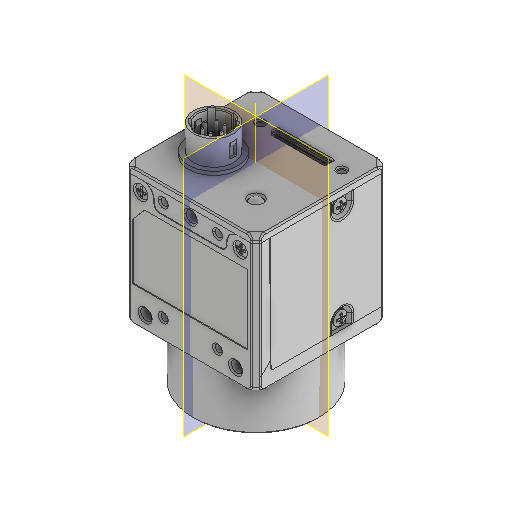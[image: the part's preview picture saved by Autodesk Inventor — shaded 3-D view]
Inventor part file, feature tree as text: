
AUTODESK INVENTOR PART (.ipt)
format: ipt  version: 2024.1 (Build 281209000, 209)  size: 3,227,136 bytes
history: native  units: mm
features: plane x2, other x1, imported_body x1
ambient origin geometry x8: Origin, YZ Plane, XZ Plane, XY Plane, X Axis, Y Axis, Z Axis, Center Point
bodies: Volumenkörper1 (feature_tree)
feature tree (4):
  plane  "Arbeitsebene1"
  plane  "Arbeitsebene2"
  other  "Arbeitsachse1"
  imported_body  "Basis1"
